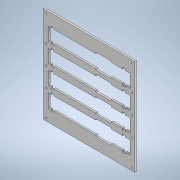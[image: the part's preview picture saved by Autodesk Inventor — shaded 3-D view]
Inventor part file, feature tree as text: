
AUTODESK INVENTOR PART (.ipt)
format: ipt  version: 2021 (Build 250183000, 183)  size: 264,192 bytes
history: native  units: mm
features: sketch x4, extrude x3, projected_geometry x2, pattern_linear x1, hole x1
ambient origin geometry x8: Origin, YZ Plane, XZ Plane, XY Plane, X Axis, Y Axis, Z Axis, Center Point
bodies: Solid1 (feature_tree)
feature tree (11):
  extrude  "Extrusion1"  Depth=110.0mm
  pattern_linear  "Rectangular Pattern1"  Count1=11  [1 undecoded]
  extrude  "Extrusion2"  Depth=82.0mm
  extrude  "Extrusion3"  Depth=40.0mm
  hole  "Hole1"  [1 undecoded]
  sketch  "Sketch1"  dims[d0=1.0mm d1=4.0mm d2=110.0mm]
  sketch  "Sketch2"  dims[d3=40.4mm d5=82.0mm]
  sketch  "Sketch3"  dims[d6=3.5mm d7=0.0mm d8=40.0mm d10=40.4mm]
  sketch  "Sketch4"  dims[d11=20.0mm d12=0.0mm d13=20.0mm d14=0.0mm d15=6.0mm d16=6.0mm d17=6.0mm d18=6.0mm d19=6.0mm d20=6.0mm d21=3.4mm d22=6.0mm d23=6.3mm d24=2.0mm d25=90.0deg d26=8.0mm d27=20.594885mm d32=144.5mm d33=0.0mm d37=5.5mm d38=5.5mm d39=9.141602mm d40=4.8046mm]
  projected_geometry  "Project Cut Edges1"
  projected_geometry  "Project Cut Edges2"
note: 2 required parameter values undecoded (feature->parameter linkage not recoverable at this tier; creation-order binding heuristic only, values carry confidence <= 0.55)
